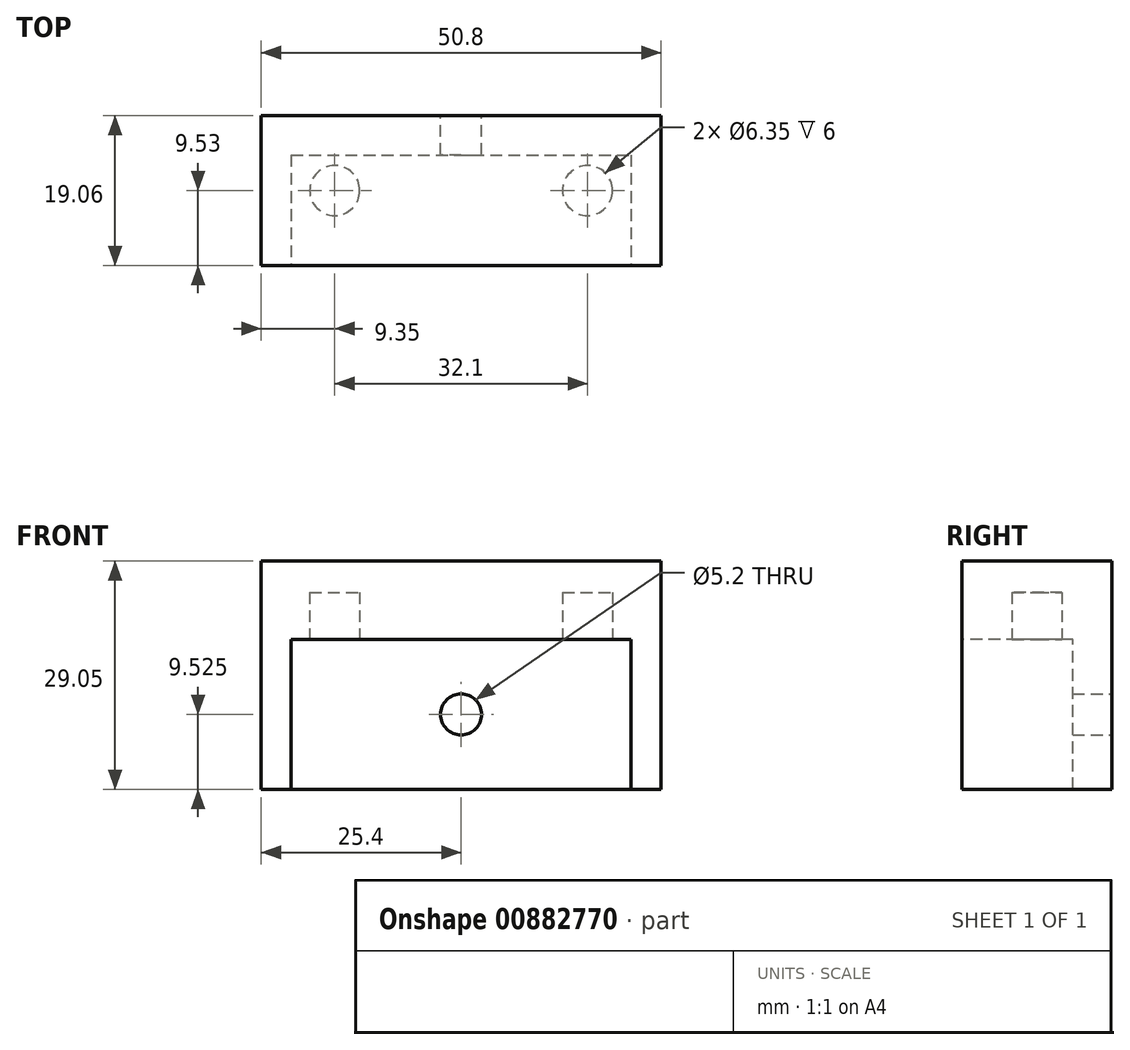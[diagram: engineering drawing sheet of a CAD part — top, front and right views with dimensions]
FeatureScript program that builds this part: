
annotation { "Feature Type Name" : "Feature", "Feature Type Description" : "" }
export const myFeature = defineFeature(function(context is Context, id is Id, definition is map)
    precondition{}
    {
        {
            var Q0;
            Q0=qCreatedBy(makeId("Top.planeOp"),FACE);
            var sketch = newSketch(context, id + "F0", { "sketchPlane" : qUnion([Q0])});
            skLineSegment(sketch, "E0.bottom", {"start": v(25.4, -9.52) * mm, "end": v(-25.4, -9.53) * mm});
            skLineSegment(sketch, "E0.top", {"start": v(25.4, 9.53) * mm, "end": v(-25.4, 9.52) * mm});
            skLineSegment(sketch, "E0.left", {"start": v(25.4, -9.52) * mm, "end": v(25.4, 9.53) * mm});
            skLineSegment(sketch, "E0.right", {"start": v(-25.4, -9.53) * mm, "end": v(-25.4, 9.52) * mm});
            skPoint(sketch, "E0.middle", {"position": v(0, 0) * mm});
            skSolve(sketch);
        }
        {
            var Q0;
            Q0 = qSketchRegion(id + "F0", true);
            extrude(context, id + "F1", {"entities" : qUnion([Q0]), "depth" : 10 * mm, "offsetDistance" : 25.4 * mm});
        }
        {
            var Q0;
            Q0=makeQuery(id+"F1.opExtrude","CAP_FACE",FACE,{"disambiguationData":[OSD([sQuery(id+"F0.wireOp",EDGE,"E0.bottom"),sQuery(id+"F0.wireOp",EDGE,"E0.top"),sQuery(id+"F0.wireOp",EDGE,"E0.left"),sQuery(id+"F0.wireOp",EDGE,"E0.right")])],"isStart":true});
            var sketch = newSketch(context, id + "F2", { "sketchPlane" : qUnion([Q0])});
            skLineSegment(sketch, "E1", {"start": v(-25.4, 0) * mm, "end": v(25.4, 0) * mm});
            skLineSegment(sketch, "E2", {"start": v(0, 9.53) * mm, "end": v(0, -9.53) * mm});
            skCircle(sketch, "E3", {"center": v(-16.05, 0) * mm, "radius": 3.18 * mm});
            skCircle(sketch, "E4", {"center": v(16.05, 0) * mm, "radius": 3.18 * mm});
            skSolve(sketch);
        }
        {
            var Q0;
            Q0 = qSketchRegion(id + "F2", true);
            extrude(context, id + "F3", {"entities" : qUnion([Q0]), "operationType" : NewBodyOperationType.REMOVE, "oppositeDirection" : true, "depth" : 6 * mm, "offsetDistance" : 25.4 * mm});
        }
        {
            var Q0;
            Q0=makeQuery(id+"F1.opExtrude","CAP_FACE",FACE,{"disambiguationData":[OSD([sQuery(id+"F0.wireOp",EDGE,"E0.bottom"),sQuery(id+"F0.wireOp",EDGE,"E0.top"),sQuery(id+"F0.wireOp",EDGE,"E0.left"),sQuery(id+"F0.wireOp",EDGE,"E0.right")])],"isStart":true});
            var sketch = newSketch(context, id + "F4", { "sketchPlane" : qUnion([Q0])});
            skLineSegment(sketch, "E5.top", {"start": v(-25.4, -9.53) * mm, "end": v(25.4, -9.53) * mm});
            skLineSegment(sketch, "E5.left", {"start": v(-25.4, -4.53) * mm, "end": v(-25.4, -9.53) * mm});
            skLineSegment(sketch, "E5.right", {"start": v(25.4, -4.53) * mm, "end": v(25.4, -9.53) * mm});
            skLineSegment(sketch, "E6.bottom", {"start": v(-21.59, -4.53) * mm, "end": v(-2.5, -4.53) * mm});
            skLineSegment(sketch, "E7.top", {"start": v(-2.5, -9.53) * mm, "end": v(2.5, -9.53) * mm});
            skPoint(sketch, "E8.orphan", {"position": v(25.4, 9.53) * mm});
            skPoint(sketch, "E9.orphan", {"position": v(-25.4, 9.53) * mm});
            skLineSegment(sketch, "E10.trimOffspring", {"start": v(-2.5, -4.53) * mm, "end": v(21.59, -4.53) * mm});
            skLineSegment(sketch, "E11.top", {"start": v(25.4, 9.53) * mm, "end": v(21.59, 9.53) * mm});
            skLineSegment(sketch, "E11.left", {"start": v(25.4, -4.53) * mm, "end": v(25.4, 9.53) * mm});
            skLineSegment(sketch, "E11.right", {"start": v(21.59, -4.53) * mm, "end": v(21.59, 9.53) * mm});
            skLineSegment(sketch, "E12.top", {"start": v(-25.4, 9.53) * mm, "end": v(-21.59, 9.53) * mm});
            skLineSegment(sketch, "E12.left", {"start": v(-25.4, -4.53) * mm, "end": v(-25.4, 9.53) * mm});
            skLineSegment(sketch, "E12.right", {"start": v(-21.59, -4.53) * mm, "end": v(-21.59, 9.53) * mm});
            skSolve(sketch);
        }
        {
            var Q0;
            Q0 = qSketchRegion(id + "F4", true);
            extrude(context, id + "F5", {"entities" : qUnion([Q0]), "operationType" : NewBodyOperationType.ADD, "depth" : 19.05 * mm, "offsetDistance" : 25.4 * mm});
        }
        {
            var Q0;
            Q0=makeQuery(id+"F5.boolean.opBoolean","MERGE",FACE,{"derivedFrom":[makeQuery(id+"F1.opExtrude","SWEPT_FACE",FACE,{"disambiguationData":[OSD([sQuery(id+"F0.wireOp",EDGE,"E0.top")])]}),makeQuery(id+"F5.opExtrude","SWEPT_FACE",FACE,{"disambiguationData":[OSD([sQuery(id+"F4.wireOp",EDGE,"E5.top"),sQuery(id+"F4.wireOp",EDGE,"E7.top")])]})]});
            var sketch = newSketch(context, id + "F6", { "sketchPlane" : qUnion([Q0])});
            skCircle(sketch, "E13", {"center": v(0, -9.53) * mm, "radius": 2.6 * mm});
            skLineSegment(sketch, "E14", {"start": v(0, 0) * mm, "end": v(0, -19.05) * mm});
            skLineSegment(sketch, "E15", {"start": v(-22.09, -9.53) * mm, "end": v(28.06, -9.52) * mm});
            skSolve(sketch);
        }
        {
            var Q0;
            Q0 = qSketchRegion(id + "F6", true);
            extrude(context, id + "F7", {"entities" : qUnion([Q0]), "operationType" : NewBodyOperationType.REMOVE, "endBound" : BoundingType.UP_TO_NEXT, "oppositeDirection" : true, "depth" : 25.4 * mm, "offsetDistance" : 25.4 * mm});
        }
    });
